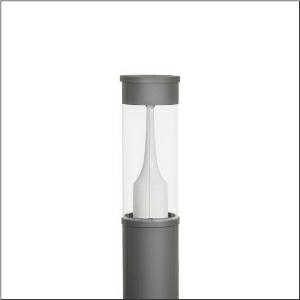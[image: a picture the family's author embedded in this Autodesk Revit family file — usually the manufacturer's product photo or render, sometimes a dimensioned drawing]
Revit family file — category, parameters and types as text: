
# Revit family: city-light_120_iq___p1_0a_5xa5285lf14h_baf3
name_source: partatom
category: Lighting Fixtures
units: mm (PartAtom-declared; Revit-internal decimal feet)

## family parameters
Cut with Voids When Loaded = No
Host = Face
Light Source = No
Part Type = Normal
Room Calculation Point = No
Round Connector Dimension = Use Diameter
Shared = No

## types (1)
- --- (1 x LED, 1510 lm, 10 W, 4000K)
    Apparent Load = 10 VA
    CIE Flux Codes = 32 61 90 93 100
    Color Rendering = 70
    Color Temperature = 4000K
    Default Elevation = 1800 mm
    Description = City-Light 120 iQ, bollard luminaire, Module 540 iQ-SR, primary light control with 3 zone facetted reflector, of plastic, silver coated, highly specular, structured, primary optical cover: cover, of PMMA, transparent, partly coated, light distribution: P1.0a, primary light characteristic: strongly asymmetric, LED, High Power LED, rated luminous flux: 1.510lm, luminous efficacy: 151lm/W, light colour: 740, colour temperature: 4000K, control gear: ECG iQ, control: presetting dimming logarithmic, Street-Remote, Auto-Match, Temp-Guard, Lumen-Switch, Night-Set, Smart-Wire, Light-Fading, Desk-Remote (wireless, voltage-free reading and setting of iQ features in the workshop via application-optimized NFC function/RFID function), optimised constant luminous flux control (CLO 2.0), with terminal, 6-pole, max. 2.5mm², mains connection: 220..240V, AC, 50/60Hz, start of lifetime: 10W, end of lifetime: 10W, reduction: 5W, luminaire housing, cylindrical, of extruded aluminium section, coated, Siteco® metallic grey (DB 702S), length: 1.200mm, diameter: 200mm, Module 540 iQ-SR, traffic white (RAL 9016), equipment: standard, protection rating (complete): IP54, insulation class (complete): insulation class II (safety insulation), certification: CE, ENEC, VDE, packaging unit: 1 piece

Light Distribution: P1.0a
    Height = 500 mm
    Lamp = 1 x LED
    Lamp Light Flux = 1510 lm
    Lamp Power = 10 W
    Lamp count = 1
    Length = 200 mm  [stored 0.656168 ft]
    Luminous efficacy = 151 lm/W
    Manufacturer = Siteco
    ModVariant = No
    Model = 5XA5285LF14H
    Number of Poles = 1
    OnlyDefault = Yes
    Power Factor = 1
    Product Name = City-Light 120 iQ | P1.0a
    Product group = bollard luminaire | pylon top
    ProductGroupID = 6104
    Protection Class = Protection class II
    Protection Degree = IP 54
    RLX_Detail_Level = 1
    RlxData = <blob elided: 52293 chars, md5=296f3617>
    Socket = socket
    Standby Power = 0 W
    System Light Flux = 1510 lm
    System Power = 10 W
    Type Comments = factory setting: luminous flux: 100 % | dim-lin: 254 | 401 mA
    Type Image = l_1006922.jpg
    URL = http://relux.com
    VarID = @adj_070809
    Voltage = 0 V
    Weight = 0.00 kg
    Width = 0 mm  [stored 0 ft]

note: [stored X ft] marks values corroborated as IEEE doubles in the binary element streams (Revit-internal decimal feet)

## geometry (parser evidence)
native form markers: Blend x4, Sweep x11
no freeform markers — native parametric forms only
